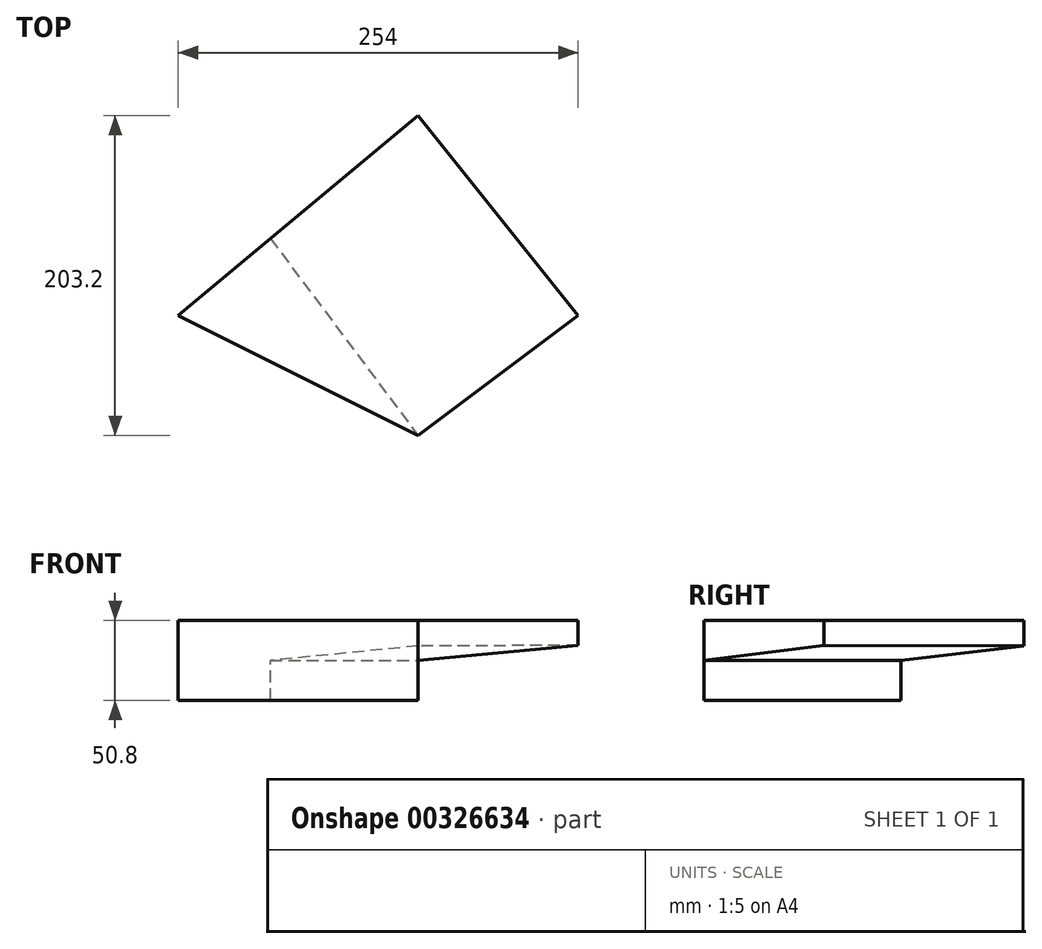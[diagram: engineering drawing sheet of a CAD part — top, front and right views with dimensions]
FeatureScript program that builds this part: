
annotation { "Feature Type Name" : "Feature", "Feature Type Description" : "" }
export const myFeature = defineFeature(function(context is Context, id is Id, definition is map)
    precondition{}
    {
        {
            var Q0;
            Q0=qCreatedBy(makeId("Top.planeOp"),FACE);
            cPlane(context, id + "F0", {"entities" : qUnion([Q0]), "cplaneType" : CPlaneType.OFFSET, "offset" : 25.4 * mm, "width" : 152.4 * mm, "height" : 152.4 * mm});
        }
        {
            var Q0;
            Q0=qCreatedBy(id+"F0.planeOp",FACE);
            var sketch = newSketch(context, id + "F1", { "sketchPlane" : qUnion([Q0])});
            skLineSegment(sketch, "E0", {"start": v(-152.4, 0) * mm, "end": v(0, 127) * mm});
            skLineSegment(sketch, "E1", {"start": v(0, 127) * mm, "end": v(101.6, 0) * mm});
            skLineSegment(sketch, "E2", {"start": v(101.6, 0) * mm, "end": v(0, -76.2) * mm});
            skLineSegment(sketch, "E3", {"start": v(0, -76.2) * mm, "end": v(-152.4, 0) * mm});
            skSolve(sketch);
        }
        {
            var Q0;
            Q0 = qSketchRegion(id + "F1", true);
            extrude(context, id + "F2", {"entities" : qUnion([Q0]), "depth" : 50.8 * mm});
        }
        {
            var Q0;
            Q0=makeQuery(id+"F2.opExtrude","SWEPT_FACE",FACE,{"disambiguationData":[OSD([sQuery(id+"F1.wireOp",EDGE,"E2")])]});
            var sketch = newSketch(context, id + "F3", { "sketchPlane" : qUnion([Q0])});
            skLineSegment(sketch, "E4", {"start": v(294.29, 25.4) * mm, "end": v(-45.72, 25.4) * mm});
            skLineSegment(sketch, "E5", {"start": v(-45.72, 25.4) * mm, "end": v(-45.72, 50.8) * mm});
            skLineSegment(sketch, "E6", {"start": v(-45.72, 50.8) * mm, "end": v(293.71, 76.2) * mm});
            skLineSegment(sketch, "E7", {"start": v(293.71, 76.2) * mm, "end": v(294.29, 25.4) * mm});
            skSolve(sketch);
        }
        {
            var Q0;
            Q0 = qSketchRegion(id + "F3", true);
            extrude(context, id + "F4", {"entities" : qUnion([Q0]), "operationType" : NewBodyOperationType.REMOVE, "endBound" : BoundingType.THROUGH_ALL, "oppositeDirection" : true, "depth" : 25.4 * mm});
        }
    });
